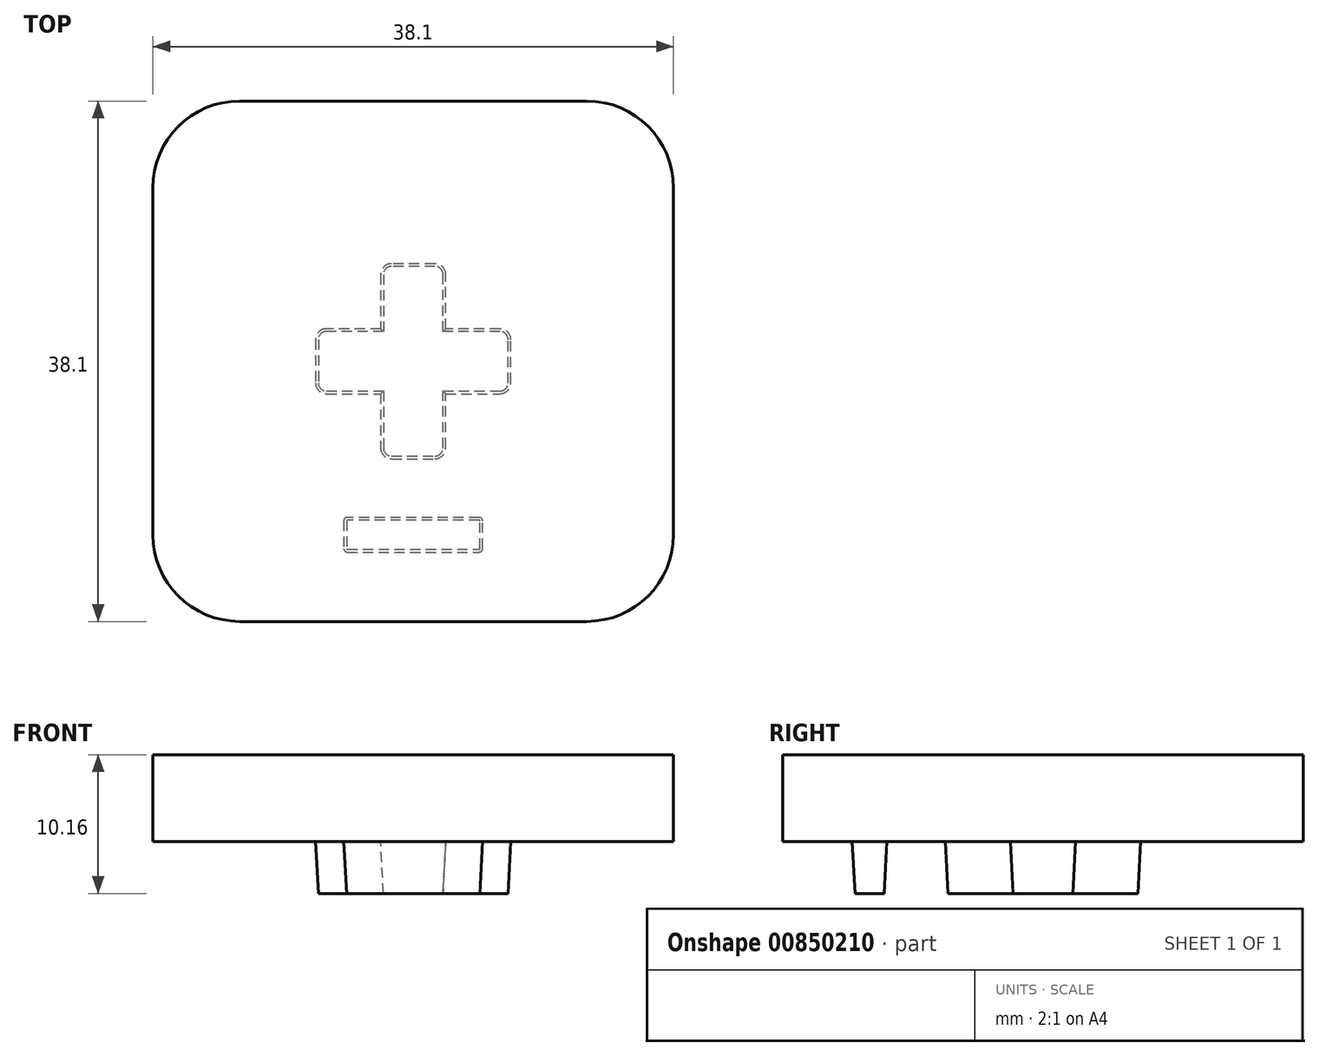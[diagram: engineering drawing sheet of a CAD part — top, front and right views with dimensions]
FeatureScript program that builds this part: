
annotation { "Feature Type Name" : "Feature", "Feature Type Description" : "" }
export const myFeature = defineFeature(function(context is Context, id is Id, definition is map)
    precondition{}
    {
        {
            var Q0;
            Q0=qCreatedBy(makeId("Top.planeOp"),FACE);
            var sketch = newSketch(context, id + "F0", { "sketchPlane" : qUnion([Q0])});
            skLineSegment(sketch, "E0.bottom", {"start": v(-12.7, 19.05) * mm, "end": v(12.7, 19.05) * mm});
            skLineSegment(sketch, "E0.top", {"start": v(-12.7, -19.05) * mm, "end": v(12.7, -19.05) * mm});
            skLineSegment(sketch, "E0.left", {"start": v(-19.05, 12.7) * mm, "end": v(-19.05, -12.7) * mm});
            skLineSegment(sketch, "E0.right", {"start": v(19.05, 12.7) * mm, "end": v(19.05, -12.7) * mm});
            skPoint(sketch, "E0.middle", {"position": v(0, 0) * mm});
            skPoint(sketch, "E1.visualSharp", {"position": v(-19.05, 19.05) * mm});
            skArc(sketch, "E1.filletArc", {"start": v(-12.7, 19.05) * mm, "mid": v(-17.2, 17.2) * mm, "end": v(-19.05, 12.7) * mm});
            skPoint(sketch, "E2.visualSharp", {"position": v(19.05, 19.05) * mm});
            skArc(sketch, "E2.filletArc", {"start": v(19.05, 12.7) * mm, "mid": v(17.2, 17.2) * mm, "end": v(12.7, 19.05) * mm});
            skPoint(sketch, "E3.visualSharp", {"position": v(-19.05, -19.05) * mm});
            skArc(sketch, "E3.filletArc", {"start": v(-19.05, -12.7) * mm, "mid": v(-17.2, -17.2) * mm, "end": v(-12.7, -19.05) * mm});
            skPoint(sketch, "E4.visualSharp", {"position": v(19.05, -19.05) * mm});
            skArc(sketch, "E4.filletArc", {"start": v(12.7, -19.05) * mm, "mid": v(17.2, -17.2) * mm, "end": v(19.05, -12.7) * mm});
            skSolve(sketch);
        }
        {
            var Q0;
            Q0 = qSketchRegion(id + "F0", true);
            extrude(context, id + "F1", {"entities" : qUnion([Q0]), "depth" : 6.35 * mm, "offsetDistance" : 25.4 * mm});
        }
        {
            var Q0;
            Q0=qCreatedBy(makeId("Top.planeOp"),FACE);
            var sketch = newSketch(context, id + "F2", { "sketchPlane" : qUnion([Q0])});
            skLineSegment(sketch, "E5.bottom", {"start": v(1.59, 7.14) * mm, "end": v(-1.59, 7.14) * mm});
            skLineSegment(sketch, "E5.top", {"start": v(1.59, -7.14) * mm, "end": v(-1.59, -7.14) * mm});
            skLineSegment(sketch, "E5.left", {"start": v(2.38, 6.35) * mm, "end": v(2.38, 2.38) * mm});
            skLineSegment(sketch, "E5.right", {"start": v(-2.38, 6.35) * mm, "end": v(-2.38, 2.38) * mm});
            skPoint(sketch, "E5.middle", {"position": v(0, 0) * mm});
            skLineSegment(sketch, "E6.bottom", {"start": v(6.35, 2.38) * mm, "end": v(2.38, 2.38) * mm});
            skLineSegment(sketch, "E6.top", {"start": v(6.35, -2.38) * mm, "end": v(2.38, -2.38) * mm});
            skLineSegment(sketch, "E6.left", {"start": v(7.14, 1.59) * mm, "end": v(7.14, -1.59) * mm});
            skLineSegment(sketch, "E6.right", {"start": v(-7.14, 1.59) * mm, "end": v(-7.14, -1.59) * mm});
            skPoint(sketch, "E7.visualSharp", {"position": v(-2.38, 7.14) * mm});
            skArc(sketch, "E7.filletArc", {"start": v(-1.59, 7.14) * mm, "mid": v(-2.15, 6.91) * mm, "end": v(-2.38, 6.35) * mm});
            skPoint(sketch, "E8.visualSharp", {"position": v(2.38, 7.14) * mm});
            skArc(sketch, "E8.filletArc", {"start": v(2.38, 6.35) * mm, "mid": v(2.15, 6.91) * mm, "end": v(1.59, 7.14) * mm});
            skPoint(sketch, "E9.visualSharp", {"position": v(7.14, 2.38) * mm});
            skArc(sketch, "E9.filletArc", {"start": v(7.14, 1.59) * mm, "mid": v(6.91, 2.15) * mm, "end": v(6.35, 2.38) * mm});
            skPoint(sketch, "E10.visualSharp", {"position": v(7.14, -2.38) * mm});
            skArc(sketch, "E10.filletArc", {"start": v(6.35, -2.38) * mm, "mid": v(6.91, -2.15) * mm, "end": v(7.14, -1.59) * mm});
            skPoint(sketch, "E11.visualSharp", {"position": v(2.38, -7.14) * mm});
            skArc(sketch, "E11.filletArc", {"start": v(1.59, -7.14) * mm, "mid": v(2.15, -6.91) * mm, "end": v(2.38, -6.35) * mm});
            skPoint(sketch, "E12.visualSharp", {"position": v(-2.38, -7.14) * mm});
            skArc(sketch, "E12.filletArc", {"start": v(-2.38, -6.35) * mm, "mid": v(-2.15, -6.91) * mm, "end": v(-1.59, -7.14) * mm});
            skPoint(sketch, "E13.visualSharp", {"position": v(-7.14, -2.38) * mm});
            skArc(sketch, "E13.filletArc", {"start": v(-7.14, -1.59) * mm, "mid": v(-6.91, -2.15) * mm, "end": v(-6.35, -2.38) * mm});
            skPoint(sketch, "E14.visualSharp", {"position": v(-7.14, 2.38) * mm});
            skArc(sketch, "E14.filletArc", {"start": v(-6.35, 2.38) * mm, "mid": v(-6.91, 2.15) * mm, "end": v(-7.14, 1.59) * mm});
            skLineSegment(sketch, "E15.trimOffspring", {"start": v(-2.38, 2.38) * mm, "end": v(-6.35, 2.38) * mm});
            skLineSegment(sketch, "E16.trimOffspring", {"start": v(-2.38, -2.38) * mm, "end": v(-2.38, -6.35) * mm});
            skLineSegment(sketch, "E17.trimOffspring", {"start": v(2.38, -2.38) * mm, "end": v(2.38, -6.35) * mm});
            skLineSegment(sketch, "E18.trimOffspring", {"start": v(-2.38, -2.38) * mm, "end": v(-6.35, -2.38) * mm});
            skLineSegment(sketch, "E19", {"start": v(0, 0) * mm, "end": v(0, -12.7) * mm, "construction": true});
            skPoint(sketch, "E19.endSnap0", {"position": v(0, -7.14) * mm});
            skLineSegment(sketch, "E20.bottom", {"start": v(4.83, -11.43) * mm, "end": v(-4.83, -11.43) * mm});
            skLineSegment(sketch, "E20.top", {"start": v(4.83, -13.97) * mm, "end": v(-4.83, -13.97) * mm});
            skLineSegment(sketch, "E20.left", {"start": v(5.08, -11.68) * mm, "end": v(5.08, -13.72) * mm});
            skLineSegment(sketch, "E20.right", {"start": v(-5.08, -11.68) * mm, "end": v(-5.08, -13.72) * mm});
            skPoint(sketch, "E20.middle", {"position": v(0, -12.7) * mm});
            skPoint(sketch, "E21.visualSharp", {"position": v(-5.08, -13.97) * mm});
            skArc(sketch, "E21.filletArc", {"start": v(-5.08, -13.72) * mm, "mid": v(-5, -13.9) * mm, "end": v(-4.83, -13.97) * mm});
            skPoint(sketch, "E22.visualSharp", {"position": v(-5.08, -11.43) * mm});
            skArc(sketch, "E22.filletArc", {"start": v(-4.83, -11.43) * mm, "mid": v(-5, -11.5) * mm, "end": v(-5.08, -11.68) * mm});
            skPoint(sketch, "E23.visualSharp", {"position": v(5.08, -11.43) * mm});
            skArc(sketch, "E23.filletArc", {"start": v(5.08, -11.68) * mm, "mid": v(5, -11.5) * mm, "end": v(4.83, -11.43) * mm});
            skPoint(sketch, "E24.visualSharp", {"position": v(5.08, -13.97) * mm});
            skArc(sketch, "E24.filletArc", {"start": v(4.83, -13.97) * mm, "mid": v(5, -13.9) * mm, "end": v(5.08, -13.72) * mm});
            skSolve(sketch);
        }
        {
            var Q0;
            Q0 = qSketchRegion(id + "F2", true);
            extrude(context, id + "F3", {"entities" : qUnion([Q0]), "operationType" : NewBodyOperationType.ADD, "oppositeDirection" : true, "depth" : 3.8 * mm, "offsetDistance" : 25.4 * mm, "hasDraft" : true, "draftAngle" : 3 * degree, "draftPullDirection" : true});
        }
    });
